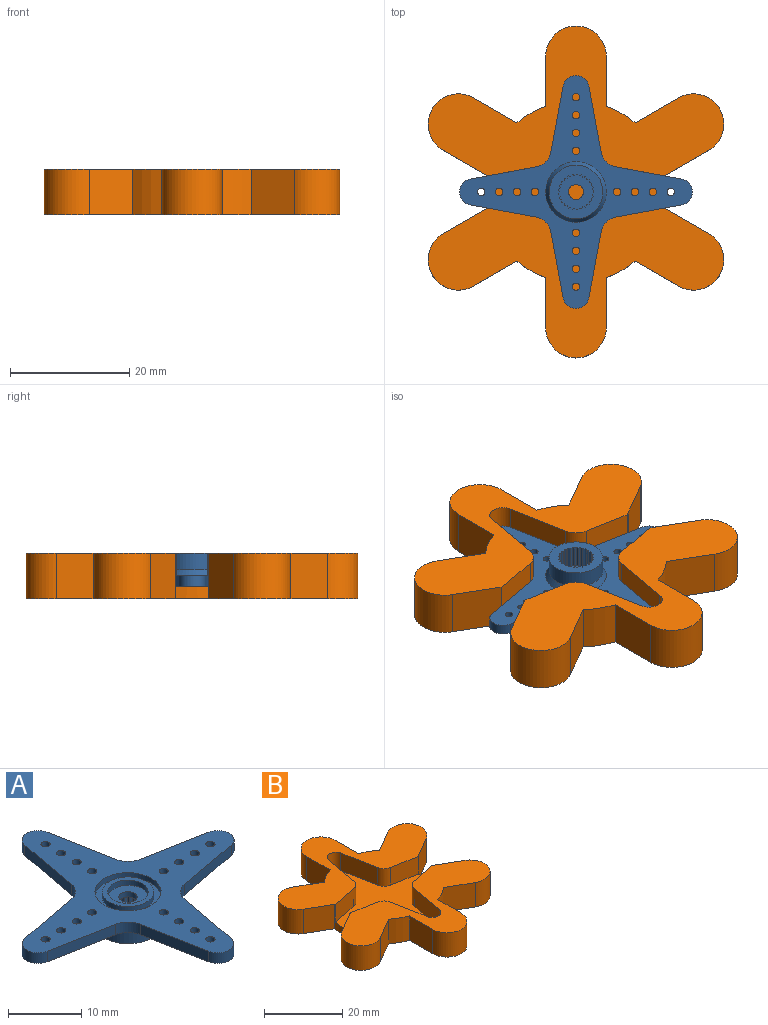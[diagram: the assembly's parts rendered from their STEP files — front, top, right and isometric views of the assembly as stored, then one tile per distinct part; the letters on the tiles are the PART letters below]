
ASSEMBLY  parts=2 mates=1
PART A: 95 faces, bbox 39x39x5.5 mm
  f0: cone r=5.08mm half-angle=30deg, axis (0,0,1), area 34.7mm2, adj f22,f93
  f1: cylinder r=4.5mm len=9mm, axis (0,0,1), area 24.7mm2, adj f77,f94
  f2: cylinder r=0.63mm len=1.75mm, axis (0,0,1), area 6.9mm2, adj f93,f94
  f3: cylinder r=0.63mm len=1.75mm, axis (0,0,1), area 6.9mm2, adj f93,f94
  f4: cylinder r=0.63mm len=1.75mm, axis (0,0,1), area 6.9mm2, adj f93,f94
  f5: cylinder r=0.63mm len=1.75mm, axis (0,0,1), area 6.9mm2, adj f93,f94
  f6: cylinder r=0.63mm len=1.75mm, axis (0,0,1), area 6.9mm2, adj f93,f94
  f7: cylinder r=0.63mm len=1.75mm, axis (0,0,1), area 6.9mm2, adj f93,f94
  f8: cylinder r=0.63mm len=1.75mm, axis (0,0,1), area 6.9mm2, adj f93,f94
  f9: cylinder r=0.63mm len=1.75mm, axis (0,0,1), area 6.9mm2, adj f93,f94
  f10: cylinder r=0.63mm len=1.75mm, axis (0,0,1), area 6.9mm2, adj f93,f94
  f11: cylinder r=0.63mm len=1.75mm, axis (0,0,1), area 6.9mm2, adj f93,f94
  f12: cylinder r=0.63mm len=1.75mm, axis (0,0,1), area 6.9mm2, adj f93,f94
  f13: cylinder r=0.63mm len=1.75mm, axis (0,0,1), area 6.9mm2, adj f93,f94
  f14: cylinder r=0.63mm len=1.75mm, axis (0,0,1), area 6.9mm2, adj f93,f94
  f15: cylinder r=0.63mm len=1.75mm, axis (0,0,1), area 6.9mm2, adj f93,f94
  f16: cylinder r=0.63mm len=1.75mm, axis (0,0,1), area 6.9mm2, adj f93,f94
  f17: cylinder r=0.63mm len=1.75mm, axis (0,0,1), area 6.9mm2, adj f93,f94
  f18: cylinder r=2.2mm len=4.33mm, axis (0,0,1), area 10.7mm2, adj f81,f82,f93,f94
  f19: cylinder r=3.5mm len=7mm, axis (0,0,1), area 19.2mm2, adj f23,f77
  f20: cylinder r=2.75mm len=5.5mm, axis (0,0,1), area 15.1mm2, adj f23,f76
  f21: cylinder r=1.25mm len=2.5mm, axis (0,0,-1), area 6.9mm2, adj f75,f76
  f22: cylinder r=4.5mm len=9mm, axis (0,0,1), area 77.8mm2, adj f0,f74
  f23: plane 7x7mm, normal (0,0,1), area 14.7mm2, adj f19,f20
  f24: plane 3.75x0.34mm, normal (-0.62,-0.79,0), area 1.6mm2, adj f25,f73,f74,f75
  f25: plane 3.75x0.34mm, normal (0.62,-0.79,0), area 1.6mm2, adj f24,f26,f74,f75
  f26: plane 3.75x0.4mm, normal (-0.4,-0.91,0), area 1.6mm2, adj f25,f27,f74,f75
  f27: plane 3.75x0.35mm, normal (0.79,-0.61,0), area 1.6mm2, adj f26,f28,f74,f75
  f28: plane 3.75x0.43mm, normal (-0.16,-0.99,0), area 1.6mm2, adj f27,f29,f74,f75
  f29: plane 3.75x0.4mm, normal (0.92,-0.39,0), area 1.6mm2, adj f28,f30,f74,f75
  f30: plane 3.75x0.44mm, normal (0.09,-1,0), area 1.6mm2, adj f29,f31,f74,f75
  f31: plane 3.75x0.43mm, normal (0.99,-0.15,0), area 1.6mm2, adj f30,f32,f74,f75
  f32: plane 3.75x0.41mm, normal (0.33,-0.94,0), area 1.6mm2, adj f31,f33,f74,f75
  f33: plane 3.75x0.44mm, normal (0.99,0.1,0), area 1.6mm2, adj f32,f34,f74,f75
  f34: plane 3.75x0.37mm, normal (0.56,-0.83,0), area 1.6mm2, adj f33,f35,f74,f75
  f35: plane 3.75x0.41mm, normal (0.94,0.35,0), area 1.6mm2, adj f34,f36,f74,f75
  f36: plane 3.75x0.33mm, normal (0.74,-0.67,0), area 1.6mm2, adj f35,f37,f74,f75
  f37: plane 3.75x0.36mm, normal (0.82,0.57,0), area 1.6mm2, adj f36,f38,f74,f75
  f38: plane 3.75x0.39mm, normal (0.89,-0.46,0), area 1.6mm2, adj f37,f39,f74,f75
  f39: plane 3.75x0.33mm, normal (0.66,0.76,0), area 1.6mm2, adj f38,f40,f74,f75
  f40: plane 3.75x0.43mm, normal (0.97,-0.23,0), area 1.6mm2, adj f39,f41,f74,f75
  f41: plane 3.75x0.39mm, normal (0.45,0.89,0), area 1.6mm2, adj f40,f42,f74,f75
  f42: plane 3.75x0.44mm, normal (1,0.02,0), area 1.6mm2, adj f41,f43,f74,f75
  f43: plane 3.75x0.43mm, normal (0.21,0.98,0), area 1.6mm2, adj f42,f44,f74,f75
  f44: plane 3.75x0.42mm, normal (0.96,0.27,0), area 1.6mm2, adj f43,f45,f74,f75
  f45: plane 3.75x0.44mm, normal (-0.04,1,0), area 1.6mm2, adj f44,f46,f74,f75
  f46: plane 3.75x0.38mm, normal (0.86,0.5,0), area 1.6mm2, adj f45,f47,f74,f75
  f47: plane 3.75x0.42mm, normal (-0.29,0.96,0), area 1.6mm2, adj f46,f48,f74,f75
  f48: plane 3.75x0.31mm, normal (0.71,0.7,0), area 1.6mm2, adj f47,f49,f74,f75
  f49: plane 3.75x0.38mm, normal (-0.52,0.86,0), area 1.6mm2, adj f48,f50,f74,f75
  f50: plane 3.75x0.38mm, normal (0.52,0.86,0), area 1.6mm2, adj f49,f51,f74,f75
  f51: plane 3.75x0.31mm, normal (-0.71,0.7,0), area 1.6mm2, adj f50,f52,f74,f75
  f52: plane 3.75x0.42mm, normal (0.29,0.96,0), area 1.6mm2, adj f51,f53,f74,f75
  f53: plane 3.75x0.38mm, normal (-0.86,0.5,0), area 1.6mm2, adj f52,f54,f74,f75
  f54: plane 3.75x0.44mm, normal (0.04,1,0), area 1.6mm2, adj f53,f55,f74,f75
  f55: plane 3.75x0.42mm, normal (-0.96,0.27,0), area 1.6mm2, adj f54,f56,f74,f75
  f56: plane 3.75x0.43mm, normal (-0.21,0.98,0), area 1.6mm2, adj f55,f57,f74,f75
  f57: plane 3.75x0.44mm, normal (-1,0.02,0), area 1.6mm2, adj f56,f58,f74,f75
  f58: plane 3.75x0.39mm, normal (-0.45,0.89,0), area 1.6mm2, adj f57,f59,f74,f75
  f59: plane 3.75x0.43mm, normal (-0.97,-0.23,0), area 1.6mm2, adj f58,f60,f74,f75
  f60: plane 3.75x0.33mm, normal (-0.66,0.76,0), area 1.6mm2, adj f59,f61,f74,f75
  f61: plane 3.75x0.39mm, normal (-0.89,-0.46,0), area 1.6mm2, adj f60,f62,f74,f75
  f62: plane 3.75x0.36mm, normal (-0.82,0.57,0), area 1.6mm2, adj f61,f63,f74,f75
  f63: plane 3.75x0.33mm, normal (-0.74,-0.67,0), area 1.6mm2, adj f62,f64,f74,f75
  f64: plane 3.75x0.41mm, normal (-0.94,0.35,0), area 1.6mm2, adj f63,f65,f74,f75
  f65: plane 3.75x0.37mm, normal (-0.56,-0.83,0), area 1.6mm2, adj f64,f66,f74,f75
  f66: plane 3.75x0.44mm, normal (-0.99,0.1,0), area 1.6mm2, adj f65,f67,f74,f75
  f67: plane 3.75x0.41mm, normal (-0.33,-0.94,0), area 1.6mm2, adj f66,f68,f74,f75
  f68: plane 3.75x0.43mm, normal (-0.99,-0.15,0), area 1.6mm2, adj f67,f69,f74,f75
  f69: plane 3.75x0.44mm, normal (-0.09,-1,0), area 1.6mm2, adj f68,f70,f74,f75
  f70: plane 3.75x0.4mm, normal (-0.92,-0.39,0), area 1.6mm2, adj f69,f71,f74,f75
  f71: plane 3.75x0.43mm, normal (0.16,-0.99,0), area 1.6mm2, adj f70,f72,f74,f75
  f72: plane 3.75x0.35mm, normal (-0.79,-0.61,0), area 1.6mm2, adj f71,f73,f74,f75
  f73: plane 3.75x0.4mm, normal (0.4,-0.91,0), area 1.6mm2, adj f24,f72,f74,f75
  f74: plane 9x9mm, normal (0,0,-1), area 37.8mm2, adj f22,f24,f25,f26,f27,f28,f29,f30
  f75: plane 5.99x5.98mm, normal (0,0,-1), area 20.9mm2, adj f21,f24,f25,f26,f27,f28,f29,f30
  f76: plane 5.5x5.5mm, normal (0,0,1), area 18.8mm2, adj f20,f21
  f77: plane 9x9mm, normal (0,0,1), area 25.1mm2, adj f1,f19
  f78: cylinder r=2.2mm len=4.33mm, axis (0,0,1), area 10.7mm2, adj f79,f92,f93,f94
  f79: plane 11.08x2.06mm, normal (0.98,0.18,0), area 19.7mm2, adj f78,f80,f93,f94
  f80: cylinder r=3mm len=2.4mm, axis (0,0,1), area 6.3mm2, adj f79,f81,f93,f94
  f81: plane 11.08x2.06mm, normal (0.18,0.98,0), area 19.7mm2, adj f18,f80,f93,f94
  f82: plane 11.08x2.06mm, normal (0.18,-0.98,0), area 19.7mm2, adj f18,f83,f93,f94
  f83: cylinder r=3mm len=2.4mm, axis (0,0,1), area 6.3mm2, adj f82,f84,f93,f94
  f84: plane 11.08x2.06mm, normal (0.98,-0.18,0), area 19.7mm2, adj f83,f85,f93,f94
  f85: cylinder r=2.2mm len=4.33mm, axis (0,0,1), area 10.7mm2, adj f84,f86,f93,f94
  f86: plane 11.08x2.06mm, normal (-0.98,-0.18,0), area 19.7mm2, adj f85,f87,f93,f94
  f87: cylinder r=3mm len=2.4mm, axis (0,0,1), area 6.3mm2, adj f86,f88,f93,f94
  f88: plane 11.08x2.06mm, normal (-0.18,-0.98,0), area 19.7mm2, adj f87,f89,f93,f94
  f89: cylinder r=2.2mm len=4.33mm, axis (0,0,1), area 10.7mm2, adj f88,f90,f93,f94
  f90: plane 11.08x2.06mm, normal (-0.18,0.98,0), area 19.7mm2, adj f89,f91,f93,f94
  f91: cylinder r=3mm len=2.4mm, axis (0,0,1), area 6.3mm2, adj f90,f92,f93,f94
  f92: plane 11.08x2.06mm, normal (-0.98,0.18,0), area 19.7mm2, adj f78,f91,f93,f94
  f93: plane 39x39mm, normal (0,0,-1), area 364.6mm2, adj f0,f2,f3,f4,f5,f6,f7,f8
  f94: plane 39x39mm, normal (0,0,1), area 382mm2, adj f1,f2,f3,f4,f5,f6,f7,f8
PART B: 42 faces, bbox 49.5x55.6x7.6 mm
  f0: plane 49.52x25.14mm, normal (0,0,1), area 508.7mm2, adj f10,f11,f12,f13,f14,f15,f16,f17
  f1: plane 7.62x7.24mm, normal (0.5,0.87,0), area 63.7mm2, adj f2,f24,f25,f26
  f2: cylinder r=15.24mm len=7.62mm, axis (0,0,1), area 42.7mm2, adj f1,f3,f25,f26
  f3: plane 8.35x7.62mm, normal (-1,0,0), area 63.7mm2, adj f2,f4,f25,f26
  f4: cylinder r=5.08mm len=10.16mm, axis (0,0,1), area 121.6mm2, adj f3,f5,f25,f26
  f5: plane 8.35x7.62mm, normal (1,0,0), area 63.7mm2, adj f4,f6,f25,f26
  f6: cylinder r=15.24mm len=7.62mm, axis (0,0,1), area 42.7mm2, adj f5,f7,f25,f26
  f7: plane 7.62x7.24mm, normal (-0.5,0.87,0), area 63.7mm2, adj f6,f8,f25,f26
  f8: cylinder r=5.08mm len=9.48mm, axis (0,0,1), area 121.6mm2, adj f7,f9,f25,f26
  f9: plane 7.62x7.24mm, normal (0.5,-0.87,0), area 63.7mm2, adj f8,f10,f25,f26
  f10: cylinder r=15.24mm len=7.62mm, axis (0,0,1), area 13.2mm2, adj f0,f9,f11,f25,f26,f27,f30,f31
  f11: plane 7.62x7.24mm, normal (0.5,0.87,0), area 63.7mm2, adj f0,f10,f12,f25
  f12: cylinder r=5.08mm len=9.48mm, axis (0,0,1), area 121.6mm2, adj f0,f11,f13,f25
  f13: plane 7.62x7.24mm, normal (-0.5,-0.87,0), area 63.7mm2, adj f0,f12,f14,f25
  f14: cylinder r=15.24mm len=7.62mm, axis (0,0,1), area 42.7mm2, adj f0,f13,f15,f25
  f15: plane 8.35x7.62mm, normal (1,0,0), area 63.7mm2, adj f0,f14,f16,f25
  f16: cylinder r=5.08mm len=10.16mm, axis (0,0,1), area 121.6mm2, adj f0,f15,f17,f25
  f17: plane 8.35x7.62mm, normal (-1,0,0), area 63.7mm2, adj f0,f16,f18,f25
  f18: cylinder r=15.24mm len=7.62mm, axis (0,0,1), area 42.7mm2, adj f0,f17,f19,f25
  f19: plane 7.62x7.24mm, normal (0.5,-0.87,0), area 63.7mm2, adj f0,f18,f20,f25
  f20: cylinder r=5.08mm len=9.48mm, axis (0,0,1), area 121.6mm2, adj f0,f19,f21,f25
  f21: plane 7.62x7.24mm, normal (-0.5,0.87,0), area 63.7mm2, adj f0,f20,f22,f25
  f22: cylinder r=15.24mm len=7.62mm, axis (0,0,1), area 13.2mm2, adj f0,f21,f23,f25,f26,f27,f28,f29
  f23: plane 7.62x7.24mm, normal (-0.5,-0.87,0), area 63.7mm2, adj f22,f24,f25,f26
  f24: cylinder r=5.08mm len=9.48mm, axis (0,0,1), area 121.6mm2, adj f1,f23,f25,f26
  f25: plane 55.61x49.52mm, normal (0,0,-1), area 1446.5mm2, adj f1,f2,f3,f4,f5,f6,f7,f8
  f26: plane 49.52x25.14mm, normal (0,0,1), area 508.7mm2, adj f1,f2,f3,f4,f5,f6,f7,f8
  f27: plane 39x30.48mm, normal (0,0,1), area 429.2mm2, adj f10,f22,f28,f29,f30,f31,f32,f33
  f28: plane 8.38x5.5mm, normal (0.18,0.98,0), area 46.9mm2, adj f0,f22,f27,f41
  f29: plane 8.38x5.5mm, normal (0.18,-0.98,0), area 46.9mm2, adj f22,f26,f27,f32
  f30: plane 8.38x5.5mm, normal (-0.18,-0.98,0), area 46.9mm2, adj f10,f26,f27,f36
  f31: plane 8.38x5.5mm, normal (-0.18,0.98,0), area 46.9mm2, adj f0,f10,f27,f37
  f32: cylinder r=3mm len=5.5mm, axis (0,0,1), area 19.9mm2, adj f26,f27,f29,f33
  f33: plane 11.08x5.5mm, normal (0.98,-0.18,0), area 62mm2, adj f26,f27,f32,f34
  f34: cylinder r=2.2mm len=5.5mm, axis (0,0,1), area 33.6mm2, adj f26,f27,f33,f35
  f35: plane 11.08x5.5mm, normal (-0.98,-0.18,0), area 62mm2, adj f26,f27,f34,f36
  f36: cylinder r=3mm len=5.5mm, axis (0,0,1), area 19.9mm2, adj f26,f27,f30,f35
  f37: cylinder r=3mm len=5.5mm, axis (0,0,1), area 19.9mm2, adj f0,f27,f31,f38
  f38: plane 11.08x5.5mm, normal (-0.98,0.18,0), area 62mm2, adj f0,f27,f37,f39
  f39: cylinder r=2.2mm len=5.5mm, axis (0,0,1), area 33.6mm2, adj f0,f27,f38,f40
  f40: plane 11.08x5.5mm, normal (0.98,0.18,0), area 62mm2, adj f0,f27,f39,f41
  f41: cylinder r=3mm len=5.5mm, axis (0,0,1), area 19.9mm2, adj f0,f27,f28,f40
PLACE A rot(axis=(0.71,0.71,0),180deg) t=(-5.82,3.91,-5.25)mm
PLACE B t=(-5.82,-6.34,-1.5)mm
MATE fastened A.f0 <-> B.f10  axis (0,0,-1) through (-5.82,-6.34,-7)mm
